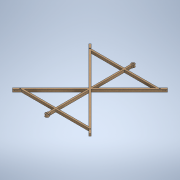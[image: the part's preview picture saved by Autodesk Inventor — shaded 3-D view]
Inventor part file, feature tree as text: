
AUTODESK INVENTOR PART (.ipt)
format: ipt  version: 2022 (Build 260153000, 153)  size: 253,952 bytes
history: native  units: mm
features: sketch x5, extrude x4, hole x2
ambient origin geometry x8: Origin, YZ Plane, XZ Plane, XY Plane, X Axis, Y Axis, Z Axis, Center Point
bodies: Body1 (feature_tree)
feature tree (11):
  sketch  "Esboço1"  dims[d5=5.0mm d6=5.0mm]
  extrude  "Extrusão2"  Depth=5.0mm
  extrude  "Extrusão3"  Depth=5.0mm
  extrude  "Extrusão4"  Depth=5.0mm
  hole  "Furo2"  [1 undecoded]
  hole  "Furo3"  [1 undecoded]
  extrude  "Extrusão5"  Depth=15.0mm
  sketch  "Esboço2"  dims[d9=5.0mm d10=5.0mm d11=5.0mm]
  sketch  "Esboço3"  dims[d12=5.0mm d15=5.0mm]
  sketch  "Esboço4"  dims[d16=5.0mm d21=5.0mm]
  sketch  "Esboço5"  dims[d22=5.0mm d27=15.0mm d28=0.0mm d33=4.0mm d34=4.0mm d35=4.0mm d36=4.0mm d37=15.0mm d38=0.0mm d39=7.0mm d40=7.0mm d41=7.0mm d42=7.0mm d43=3.0mm d44=0.0mm d52=10.0mm d53=10.0mm d54=10.0mm d55=10.0mm d56=3.0mm d57=6.0mm d58=4.0mm d59=2.0mm d60=90.0deg d61=51.2mm d62=20.594885mm d63=10.0mm d64=10.0mm d65=10.0mm d66=10.0mm d67=3.0mm d68=6.0mm d69=4.0mm d70=2.0mm d71=90.0deg d72=8.0mm d73=20.594885mm d75=22.0mm d76=15.0mm d77=8.485mm d78=3.0mm d79=40.0mm d81=360.0deg d83=22.0mm d84=8.485mm d85=3.0mm d86=40.0mm d88=360.0deg d90=15.0mm d91=15.0mm d92=0.0mm]
note: 2 required parameter values undecoded (feature->parameter linkage not recoverable at this tier; creation-order binding heuristic only, values carry confidence <= 0.55)
